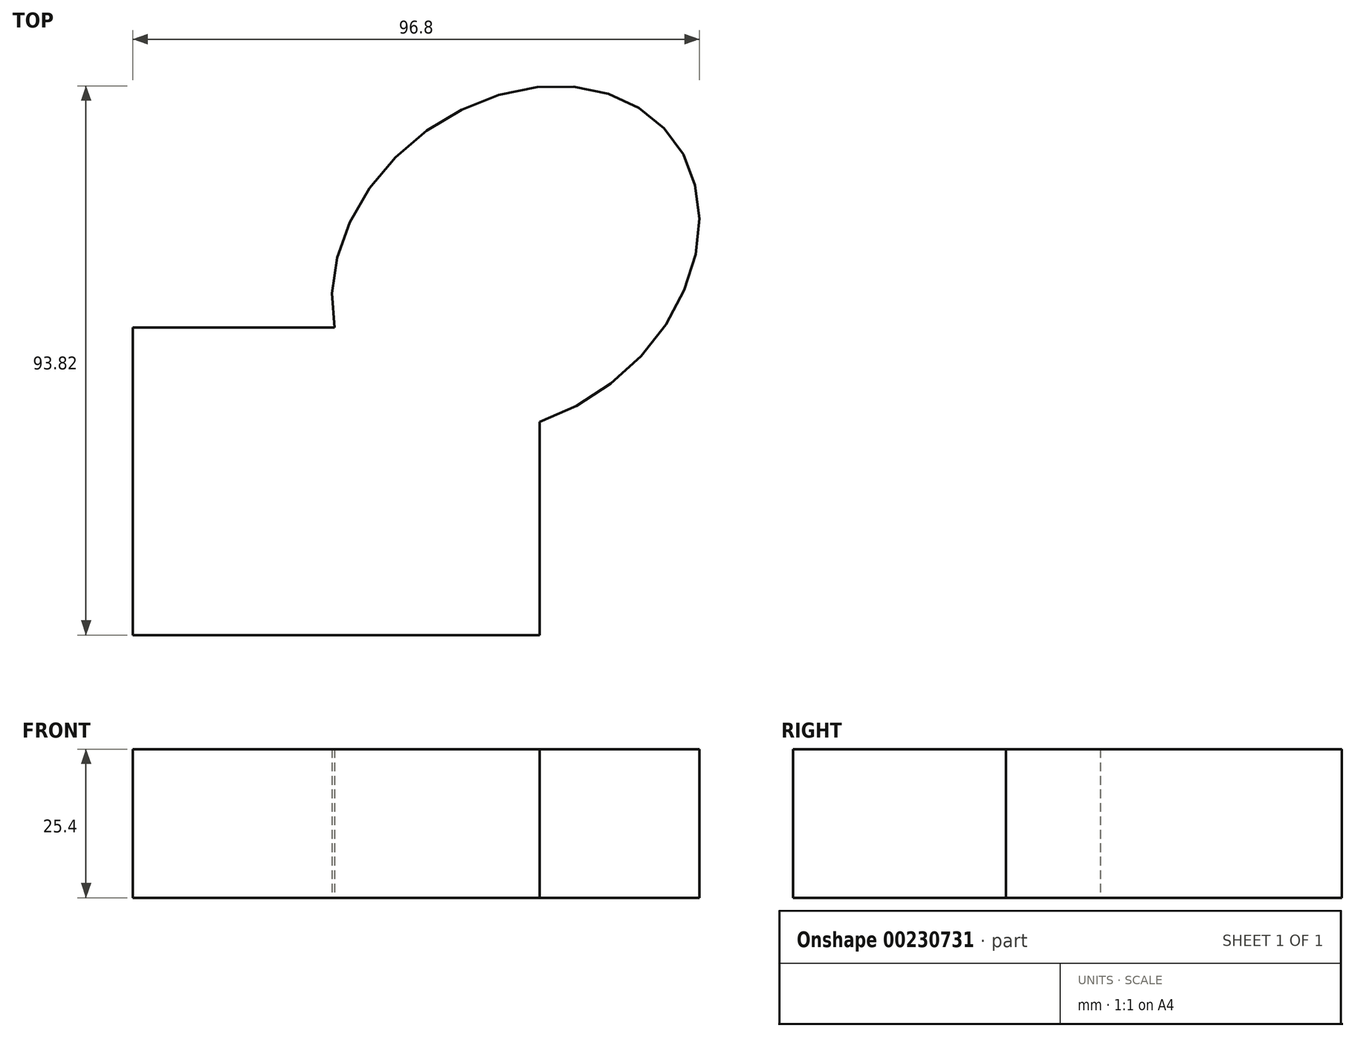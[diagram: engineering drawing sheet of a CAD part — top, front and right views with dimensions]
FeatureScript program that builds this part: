
annotation { "Feature Type Name" : "Feature", "Feature Type Description" : "" }
export const myFeature = defineFeature(function(context is Context, id is Id, definition is map)
    precondition{}
    {
        {
            var Q0;
            Q0=qCreatedBy(makeId("Top.planeOp"),FACE);
            var sketch = newSketch(context, id + "F0", { "sketchPlane" : qUnion([Q0])});
            skLineSegment(sketch, "E0.bottom", {"start": v(34.74, 26.26) * mm, "end": v(-34.74, 26.26) * mm});
            skLineSegment(sketch, "E0.top", {"start": v(34.74, -26.26) * mm, "end": v(-34.74, -26.26) * mm});
            skLineSegment(sketch, "E0.left", {"start": v(34.74, 26.26) * mm, "end": v(34.74, -26.26) * mm});
            skLineSegment(sketch, "E0.right", {"start": v(-34.74, 26.26) * mm, "end": v(-34.74, -26.26) * mm});
            skPoint(sketch, "E0.middle", {"position": v(0, 0) * mm});
            skSolve(sketch);
        }
        {
            var Q0;
            Q0=makeQuery(id+"F0.imprint","IMPRINT",FACE,{"disambiguationData":[TD([[makeQuery(id+"F0.imprint","IMPRINT",EDGE,{"derivedFrom":sQuery(id+"F0.wireOp",EDGE,"E0.bottom")}),1.0]])]});
            var sketch = newSketch(context, id + "F1", { "sketchPlane" : qUnion([Q0])});
            skEllipse(sketch, "E1", {"center": v(-29.63, 21.15) * mm, "majorRadius": 4.9 * mm, "minorRadius": 4.34 * mm, "majorAxis": v(0, -1)});
            skSolve(sketch);
        }
        {
            var Q0;
            Q0=makeQuery(id+"F0.imprint","IMPRINT",FACE,{"disambiguationData":[TD([[makeQuery(id+"F0.imprint","IMPRINT",EDGE,{"derivedFrom":sQuery(id+"F0.wireOp",EDGE,"E0.bottom")}),1.0]])]});
            var sketch = newSketch(context, id + "F2", { "sketchPlane" : qUnion([Q0])});
            skEllipse(sketch, "E2", {"center": v(25.34, 20.74) * mm, "majorRadius": 5.31 * mm, "minorRadius": 3.81 * mm, "majorAxis": v(0, -1)});
            skSolve(sketch);
        }
        {
            var Q0;
            Q0=makeQuery(id+"F0.imprint","IMPRINT",FACE,{"disambiguationData":[TD([[makeQuery(id+"F0.imprint","IMPRINT",EDGE,{"derivedFrom":sQuery(id+"F0.wireOp",EDGE,"E0.bottom")}),1.0]])]});
            var sketch = newSketch(context, id + "F3", { "sketchPlane" : qUnion([Q0])});
            skEllipse(sketch, "E3", {"center": v(30.66, 37.91) * mm, "majorRadius": 33.93 * mm, "minorRadius": 26.71 * mm, "majorAxis": v(-0.79, -0.61)});
            skSolve(sketch);
        }
        {
            var Q0;
            Q0=makeQuery(id+"F0.imprint","IMPRINT",FACE,{"disambiguationData":[TD([[makeQuery(id+"F0.imprint","IMPRINT",EDGE,{"derivedFrom":sQuery(id+"F0.wireOp",EDGE,"E0.bottom")}),1.0]])]});
            extrude(context, id + "F4", {"entities" : qUnion([Q0]), "depth" : 25.4 * mm});
        }
        {
            var Q0;
            {var subQ0=sQuery(id+"F3.wireOp",EDGE,"E3");var subQ1=makeQuery(id+"F0.imprint","IMPRINT",EDGE,{"derivedFrom":sQuery(id+"F0.wireOp",EDGE,"E0.bottom")});var subQ2=makeQuery(id+"F3.imprint","INTERSECT",VERTEX,{"derivedFrom":[subQ1,subQ0]});Q0=makeQuery(id+"F3.imprint","IMPRINT",FACE,{"disambiguationData":[TD([[makeQuery(id+"F3.imprint","IMPRINT",EDGE,{"disambiguationData":[TD([[subQ2,1.0]])],"derivedFrom":subQ0}),1.0]])]});}
            extrude(context, id + "F5", {"entities" : qUnion([Q0]), "operationType" : NewBodyOperationType.ADD, "depth" : 25.4 * mm});
        }
        {
            var Q0;
            Q0=sQuery(id+"F1.wireOp",EDGE,"E1");
            extrude(context, id + "F6", {"bodyType" : ToolBodyType.SURFACE, "surfaceEntities" : qUnion([Q0]), "depth" : 25.4 * mm});
        }
        {
            var Q0;
            Q0=sQuery(id+"F2.wireOp",EDGE,"E2");
            extrude(context, id + "F7", {"bodyType" : ToolBodyType.SURFACE, "surfaceEntities" : qUnion([Q0]), "depth" : 25.4 * mm});
        }
    });
